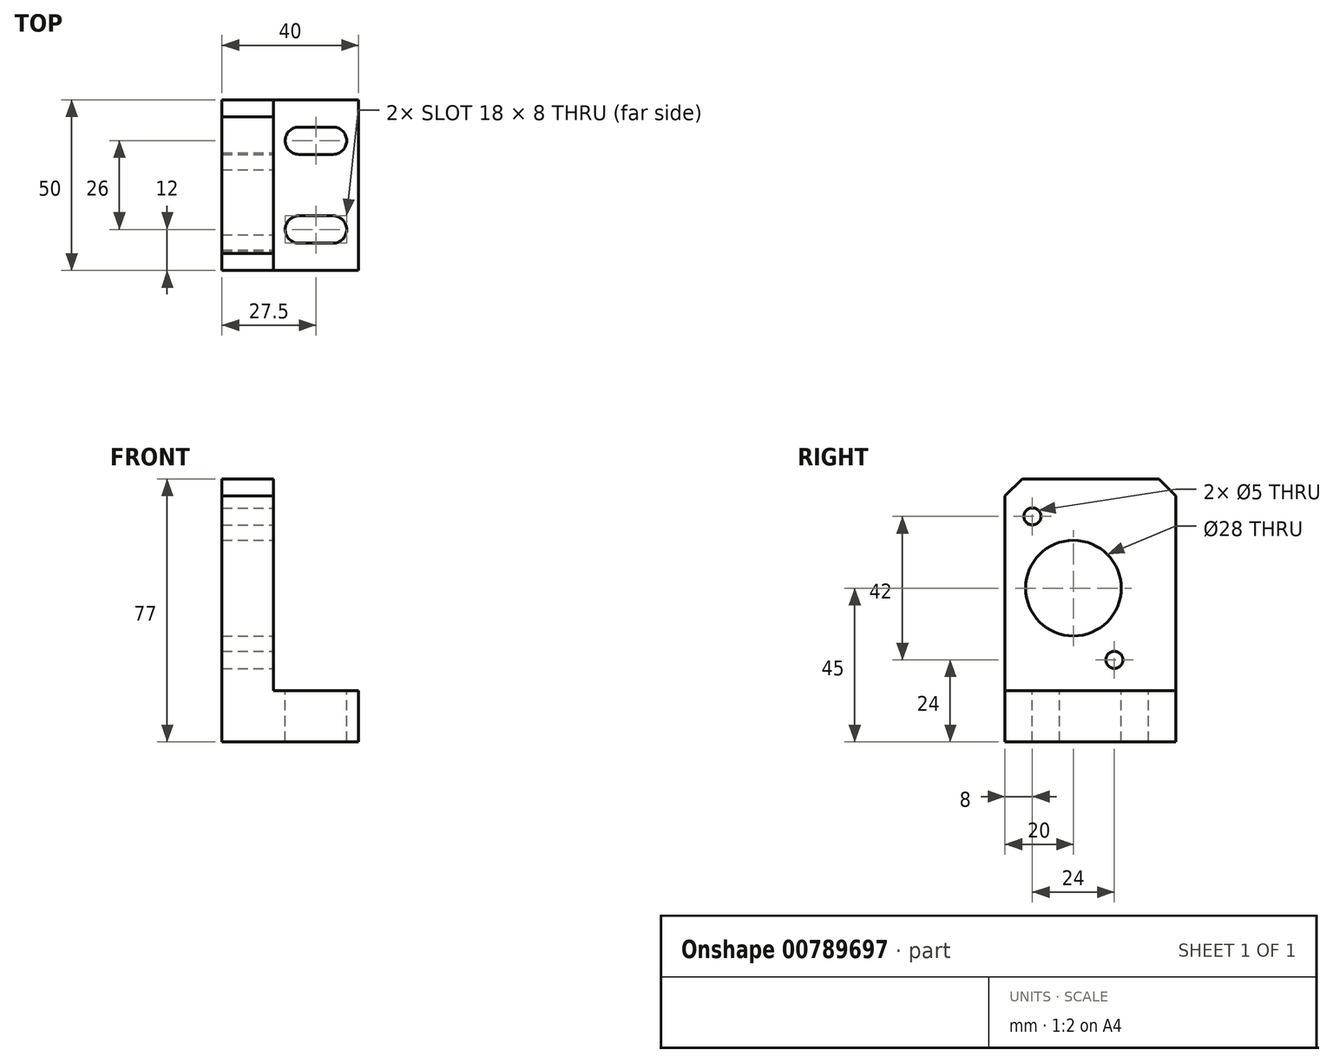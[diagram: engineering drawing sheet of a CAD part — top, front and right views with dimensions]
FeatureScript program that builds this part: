
annotation { "Feature Type Name" : "Feature", "Feature Type Description" : "" }
export const myFeature = defineFeature(function(context is Context, id is Id, definition is map)
    precondition{}
    {
        {
            var Q0;
            Q0=qCreatedBy(makeId("Top.planeOp"),FACE);
            var sketch = newSketch(context, id + "F0", { "sketchPlane" : qUnion([Q0])});
            skLineSegment(sketch, "E0.bottom", {"start": v(0, 0) * mm, "end": v(40, 0) * mm});
            skLineSegment(sketch, "E0.top", {"start": v(0, 50) * mm, "end": v(40, 50) * mm});
            skLineSegment(sketch, "E0.left", {"start": v(0, 0) * mm, "end": v(0, 50) * mm});
            skLineSegment(sketch, "E0.right", {"start": v(40, 0) * mm, "end": v(40, 50) * mm});
            skSolve(sketch);
        }
        {
            var Q0;
            Q0 = qSketchRegion(id + "F0", true);
            extrude(context, id + "F1", {"entities" : qUnion([Q0]), "depth" : 15 * mm, "offsetDistance" : 25 * mm});
        }
        {
            var Q0;
            Q0=makeQuery(id+"F1.opExtrude","CAP_FACE",FACE,{"disambiguationData":[OSD([sQuery(id+"F0.wireOp",EDGE,"E0.bottom"),sQuery(id+"F0.wireOp",EDGE,"E0.top"),sQuery(id+"F0.wireOp",EDGE,"E0.left"),sQuery(id+"F0.wireOp",EDGE,"E0.right")])],"isStart":false});
            var sketch = newSketch(context, id + "F2", { "sketchPlane" : qUnion([Q0])});
            skLineSegment(sketch, "E1.bottom", {"start": v(0, 0) * mm, "end": v(15, 0) * mm});
            skLineSegment(sketch, "E1.top", {"start": v(0, 50) * mm, "end": v(15, 50) * mm});
            skLineSegment(sketch, "E1.left", {"start": v(0, 0) * mm, "end": v(0, 50) * mm});
            skLineSegment(sketch, "E1.right", {"start": v(15, 0) * mm, "end": v(15, 50) * mm});
            skSolve(sketch);
        }
        {
            var Q0;
            Q0 = qSketchRegion(id + "F2", true);
            extrude(context, id + "F3", {"entities" : qUnion([Q0]), "operationType" : NewBodyOperationType.ADD, "depth" : 62 * mm, "offsetDistance" : 25 * mm});
        }
        {
            var Q0;
            Q0=makeQuery(id+"F3.opExtrude","SWEPT_FACE",FACE,{"disambiguationData":[OSD([sQuery(id+"F2.wireOp",EDGE,"E1.right")])]});
            var sketch = newSketch(context, id + "F4", { "sketchPlane" : qUnion([Q0])});
            skCircle(sketch, "E2", {"center": v(20, 45) * mm, "radius": 14 * mm});
            skSolve(sketch);
        }
        {
            var Q0;
            Q0 = qSketchRegion(id + "F4", true);
            extrude(context, id + "F5", {"entities" : qUnion([Q0]), "operationType" : NewBodyOperationType.REMOVE, "endBound" : BoundingType.UP_TO_NEXT, "oppositeDirection" : true, "depth" : 25 * mm, "offsetDistance" : 25 * mm});
        }
        {
            var Q0;
            Q0=makeQuery(id+"F3.opExtrude","CAP_EDGE",EDGE,{"disambiguationData":[OSD([sQuery(id+"F2.wireOp",EDGE,"E1.top")])],"isStart":false});
            var Q1;
            Q1=makeQuery(id+"F3.opExtrude","CAP_EDGE",EDGE,{"disambiguationData":[OSD([sQuery(id+"F2.wireOp",EDGE,"E1.bottom")])],"isStart":false});
            chamfer(context, id + "F6", {"entities" : qUnion([Q0, Q1]), "width" : 5 * mm, "tangentPropagation" : true});
        }
        {
            var Q0;
            Q0=makeQuery(id+"F3.opExtrude","SWEPT_FACE",FACE,{"disambiguationData":[OSD([sQuery(id+"F2.wireOp",EDGE,"E1.right")])]});
            var sketch = newSketch(context, id + "F7", { "sketchPlane" : qUnion([Q0])});
            skCircle(sketch, "E3", {"center": v(8, 66) * mm, "radius": 2.5 * mm});
            skCircle(sketch, "E4", {"center": v(32, 24) * mm, "radius": 2.5 * mm});
            skSolve(sketch);
        }
        {
            var Q0;
            Q0 = qSketchRegion(id + "F7", true);
            extrude(context, id + "F8", {"entities" : qUnion([Q0]), "operationType" : NewBodyOperationType.REMOVE, "endBound" : BoundingType.UP_TO_NEXT, "oppositeDirection" : true, "depth" : 25 * mm, "offsetDistance" : 25 * mm});
        }
        {
            var Q0;
            Q0=makeQuery(id+"F1.opExtrude","CAP_FACE",FACE,{"disambiguationData":[OSD([sQuery(id+"F0.wireOp",EDGE,"E0.bottom"),sQuery(id+"F0.wireOp",EDGE,"E0.top"),sQuery(id+"F0.wireOp",EDGE,"E0.left"),sQuery(id+"F0.wireOp",EDGE,"E0.right")])],"isStart":false});
            var sketch = newSketch(context, id + "F9", { "sketchPlane" : qUnion([Q0])});
            skLineSegment(sketch, "E5", {"start": v(22.5, 42) * mm, "end": v(32.5, 42) * mm});
            skArc(sketch, "E6", {"start": v(32.5, 34) * mm, "mid": v(36.5, 38) * mm, "end": v(32.5, 42) * mm});
            skArc(sketch, "E7", {"start": v(22.5, 42) * mm, "mid": v(18.5, 38) * mm, "end": v(22.5, 34) * mm});
            skLineSegment(sketch, "E8", {"start": v(22.5, 34) * mm, "end": v(32.5, 34) * mm});
            skLineSegment(sketch, "E9", {"start": v(22.5, 16) * mm, "end": v(32.5, 16) * mm});
            skArc(sketch, "E10", {"start": v(32.5, 8) * mm, "mid": v(36.5, 12) * mm, "end": v(32.5, 16) * mm});
            skArc(sketch, "E11", {"start": v(22.5, 16) * mm, "mid": v(18.5, 12) * mm, "end": v(22.5, 8) * mm});
            skLineSegment(sketch, "E12", {"start": v(22.5, 8) * mm, "end": v(32.5, 8) * mm});
            skSolve(sketch);
        }
        {
            var Q0;
            Q0 = qSketchRegion(id + "F9", true);
            extrude(context, id + "F10", {"entities" : qUnion([Q0]), "operationType" : NewBodyOperationType.REMOVE, "endBound" : BoundingType.UP_TO_NEXT, "oppositeDirection" : true, "depth" : 25 * mm, "offsetDistance" : 25 * mm});
        }
    });
